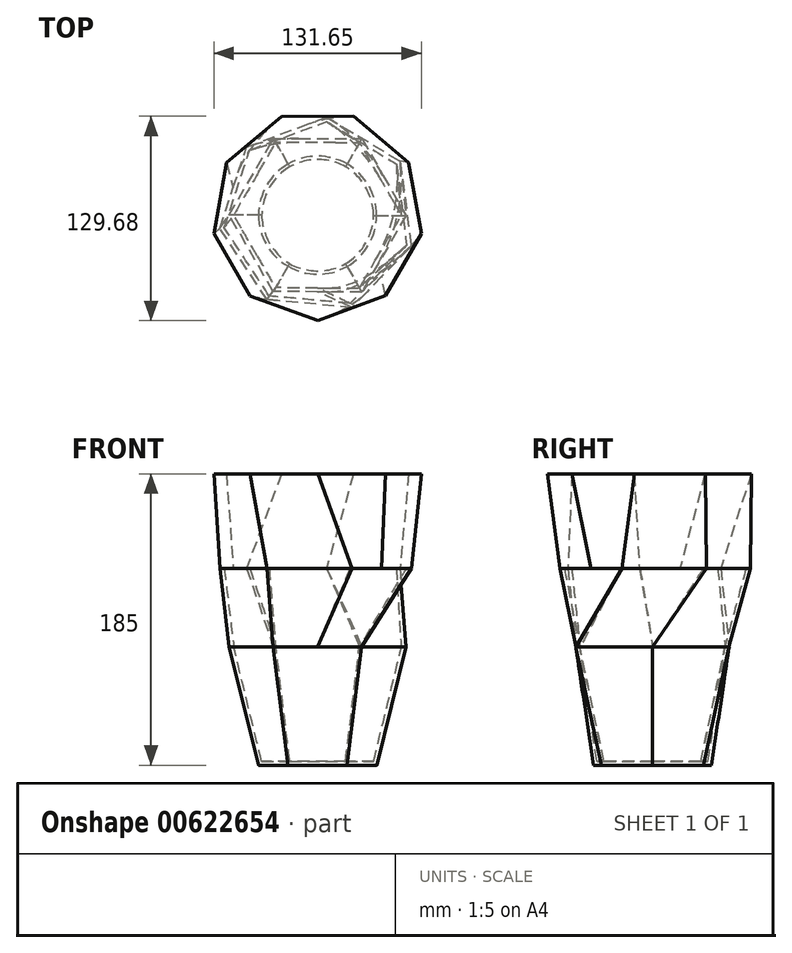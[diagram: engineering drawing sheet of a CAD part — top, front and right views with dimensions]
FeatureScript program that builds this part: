
annotation { "Feature Type Name" : "Feature", "Feature Type Description" : "" }
export const myFeature = defineFeature(function(context is Context, id is Id, definition is map)
    precondition{}
    {
        {
            var Q0;
            Q0=qCreatedBy(makeId("Top.planeOp"),FACE);
            var sketch = newSketch(context, id + "F0", { "sketchPlane" : qUnion([Q0])});
            skCircle(sketch, "E0", {"center": v(0, 0) * mm, "radius": 37.5 * mm});
            skSolve(sketch);
        }
        {
            var Q0;
            Q0=qCreatedBy(makeId("Top.planeOp"),FACE);
            cPlane(context, id + "F1", {"entities" : qUnion([Q0]), "cplaneType" : CPlaneType.OFFSET, "offset" : 75 * mm, "width" : 150 * mm, "height" : 150 * mm});
        }
        {
            var Q0;
            Q0=qCreatedBy(id+"F1.planeOp",FACE);
            var sketch = newSketch(context, id + "F2", { "sketchPlane" : qUnion([Q0])});
            skCircle(sketch, "E1.cCircle", {"center": v(0, 0) * mm, "radius": 48.63 * mm, "construction": true});
            skLineSegment(sketch, "E1.0", {"start": v(56.15, -0.18) * mm, "end": v(27.92, -48.72) * mm});
            skLineSegment(sketch, "E1.1", {"start": v(27.92, -48.72) * mm, "end": v(-28.23, -48.54) * mm});
            skLineSegment(sketch, "E1.2", {"start": v(-28.23, -48.54) * mm, "end": v(-56.15, 0.18) * mm});
            skLineSegment(sketch, "E1.3", {"start": v(-56.15, 0.18) * mm, "end": v(-27.92, 48.72) * mm});
            skLineSegment(sketch, "E1.4", {"start": v(-27.92, 48.72) * mm, "end": v(28.23, 48.54) * mm});
            skLineSegment(sketch, "E1.5", {"start": v(28.23, 48.54) * mm, "end": v(56.15, -0.18) * mm});
            skPoint(sketch, "E1.0.midPoint", {"position": v(42.04, -24.45) * mm});
            skSolve(sketch);
        }
        {
            var Q0;
            Q0 = qSketchRegion(id + "F0", true);
            var Q1;
            Q1 = qSketchRegion(id + "F2", true);
            loft(context, id + "F3", {"sheetProfilesArray" : [{ "sheetProfileEntities" : qUnion([Q0]) }, { "sheetProfileEntities" : qUnion([Q1]) }]});
        }
        {
            var Q0;
            Q0=qCreatedBy(id+"F1.planeOp",FACE);
            cPlane(context, id + "F4", {"entities" : qUnion([Q0]), "cplaneType" : CPlaneType.OFFSET, "offset" : 50 * mm, "width" : 150 * mm, "height" : 150 * mm});
        }
        {
            var Q0;
            Q0=qCreatedBy(id+"F4.planeOp",FACE);
            var sketch = newSketch(context, id + "F5", { "sketchPlane" : qUnion([Q0])});
            skCircle(sketch, "E2.cCircle", {"center": v(0, 0) * mm, "radius": 56.4 * mm, "construction": true});
            skLineSegment(sketch, "E2.0", {"start": v(5.73, 62.34) * mm, "end": v(52.31, 34.4) * mm});
            skLineSegment(sketch, "E2.1", {"start": v(52.31, 34.4) * mm, "end": v(59.5, -19.46) * mm});
            skLineSegment(sketch, "E2.2", {"start": v(59.5, -19.46) * mm, "end": v(21.89, -58.65) * mm});
            skLineSegment(sketch, "E2.3", {"start": v(21.89, -58.65) * mm, "end": v(-32.21, -53.68) * mm});
            skLineSegment(sketch, "E2.4", {"start": v(-32.21, -53.68) * mm, "end": v(-62.05, -8.29) * mm});
            skLineSegment(sketch, "E2.5", {"start": v(-62.05, -8.29) * mm, "end": v(-45.17, 43.35) * mm});
            skLineSegment(sketch, "E2.6", {"start": v(-45.17, 43.35) * mm, "end": v(5.73, 62.34) * mm});
            skPoint(sketch, "E2.0.midPoint", {"position": v(29.02, 48.37) * mm});
            skSolve(sketch);
        }
        {
            var Q1;
            Q1 = qSketchRegion(id + "F5", true);
            var Q2;
            Q2 = qSketchRegion(id + "F2", true);
            loft(context, id + "F6", {"operationType" : NewBodyOperationType.ADD, "sheetProfilesArray" : [{ "sheetProfileEntities" : qUnion([Q1]) }, { "sheetProfileEntities" : qUnion([Q2]) }]});
        }
        {
            var Q0;
            Q0=makeQuery(id+"F6.opLoft","CAP_FACE",FACE,{"disambiguationData":[OSD([makeQuery(id+"F5.imprint","IMPRINT",FACE,{"disambiguationData":[TD([[makeQuery(id+"F5.imprint","IMPRINT",EDGE,{"derivedFrom":sQuery(id+"F5.wireOp",EDGE,"E2.0")}),-1.0]])]})])],"isStart":true});
            shell(context, id + "F7", {"entities" : qUnion([Q0]), "thickness" : 2.5 * mm});
        }
        {
            var Q0;
            Q0=qCreatedBy(id+"F4.planeOp",FACE);
            cPlane(context, id + "F8", {"entities" : qUnion([Q0]), "cplaneType" : CPlaneType.OFFSET, "offset" : 60 * mm, "width" : 150 * mm, "height" : 150 * mm});
        }
        {
            var Q0;
            Q0=qCreatedBy(id+"F8.planeOp",FACE);
            var sketch = newSketch(context, id + "F9", { "sketchPlane" : qUnion([Q0])});
            skCircle(sketch, "E3.cCircle", {"center": v(0, 0) * mm, "radius": 62.8 * mm, "construction": true});
            skLineSegment(sketch, "E3.0", {"start": v(-42.89, -51.26) * mm, "end": v(-65.8, -11.7) * mm});
            skLineSegment(sketch, "E3.1", {"start": v(-65.8, -11.7) * mm, "end": v(-57.93, 33.34) * mm});
            skLineSegment(sketch, "E3.2", {"start": v(-57.93, 33.34) * mm, "end": v(-22.95, 62.77) * mm});
            skLineSegment(sketch, "E3.3", {"start": v(-22.95, 62.77) * mm, "end": v(22.77, 62.84) * mm});
            skLineSegment(sketch, "E3.4", {"start": v(22.77, 62.84) * mm, "end": v(57.84, 33.5) * mm});
            skLineSegment(sketch, "E3.5", {"start": v(57.84, 33.5) * mm, "end": v(65.84, -11.51) * mm});
            skLineSegment(sketch, "E3.6", {"start": v(65.84, -11.51) * mm, "end": v(43.04, -51.14) * mm});
            skLineSegment(sketch, "E3.7", {"start": v(43.04, -51.14) * mm, "end": v(0.1, -66.84) * mm});
            skLineSegment(sketch, "E3.8", {"start": v(0.1, -66.84) * mm, "end": v(-42.89, -51.26) * mm});
            skPoint(sketch, "E3.0.midPoint", {"position": v(-54.35, -31.48) * mm});
            skSolve(sketch);
        }
        {
            var Q1;
            Q1 = qSketchRegion(id + "F9", true);
            var Q2;
            Q2 = qSketchRegion(id + "F5", true);
            loft(context, id + "F10", {"operationType" : NewBodyOperationType.ADD, "sheetProfilesArray" : [{ "sheetProfileEntities" : qUnion([Q1]) }, { "sheetProfileEntities" : qUnion([Q2]) }]});
        }
    });
